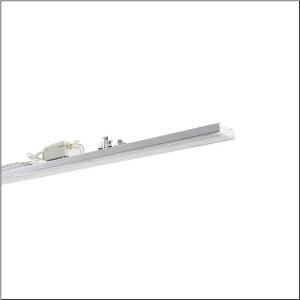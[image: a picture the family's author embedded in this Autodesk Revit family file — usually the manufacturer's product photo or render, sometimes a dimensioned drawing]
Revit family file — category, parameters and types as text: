
# Revit family: licross_r__21_recessed_ho_52tl12dn4dxm_0969
name_source: partatom
category: Lighting Fixtures
units: mm (PartAtom-declared; Revit-internal decimal feet)

## family parameters
Cut with Voids When Loaded = No
Host = Face
Light Source = No
Part Type = Normal
Room Calculation Point = No
Round Connector Dimension = Use Diameter
Shared = No

## types (1)
- --- (1 x LED, 13000 lm, 72.3 W, 4000K)
    Apparent Load = 72 VA
    CIE Flux Codes = 69 91 98 100 100
    Color Rendering = 80
    Color Temperature = 4000K
    Default Elevation = 1800 mm
    Description = Licross® 21 Recessed HO, luminaire insert, of sheet steel, galvanised, coil coated, white, length: 1.500mm, width: 66mm, height: 67mm, LED rated luminous flux: 13.000lm, light colour: 840, control gear: DALI 2, with plug, 5-pole, with phase selection, mains connection: 220..240V, AC, 50/60Hz, rated input power: 72W, halogen-free wiring, primary optical cover: cover, of PMMA, light emission: direct distribution, primary light characteristic: symmetric, protection rating (complete): IP40, insulation class (complete): insulation class I (protective earthing), certification: CE, ENEC, VDE, UKCA, protection symbol: D if used in an environment without relevant dust loads with corresponding accessories, impact resistance: IK06, permissible ambient temperature for indoor applications: -25..+35°C, corresponds to IFS (International Featured Standards) requirements for safety and quality in the food industry, reducing of maximum allowable ambient temperature of 5°C with ceiling mounting, LABS conformity tested according to VDMA 24364:2018-05, packaging unit: 1 piece
    Height = 58 mm
    Lamp = 1 x LED
    Lamp Light Flux = 13000 lm
    Lamp Power = 72.3 W
    Lamp count = 1
    Length = 1500 mm
    Luminous efficacy = 180 lm/W
    Manufacturer = Siteco
    ModVariant = No
    Model = 52TL12DN4DXM
    Mounting Place = Ceiling
    Mounting Type = Pendant
    Number of Poles = 1
    OnlyDefault = Yes
    Power Factor = 1
    Product Name = Licross® 21 Recessed HO
    Product group = luminaire insert
    ProductGroupID = 901
    Protection Class = Protection class I
    Protection Degree = IP 40
    RLX_Detail_Level = 1
    RLX_Emergency_Light_Flux = 0 lm
    RLX_Emergency_Type = 0
    RLX_Emergency_Type_DB = No
    RlxData = <blob elided: 24625 chars, md5=6f5e0a06>
    Socket = socket
    Standby Power = 0 W
    System Light Flux = 13000 lm
    System Power = 72 W
    Type Comments = factory setting: luminous flux: 100 % | dim-lin: 254 | 414 mA
    Type Image = l_1296930.jpg
    URL = http://relux.com
    VarID = @adj_046515
    Voltage = 0 V
    Weight = 0.00 kg
    Width = 66 mm

## geometry (parser evidence)
native form markers: Blend x4, Sweep x13
no freeform markers — native parametric forms only
